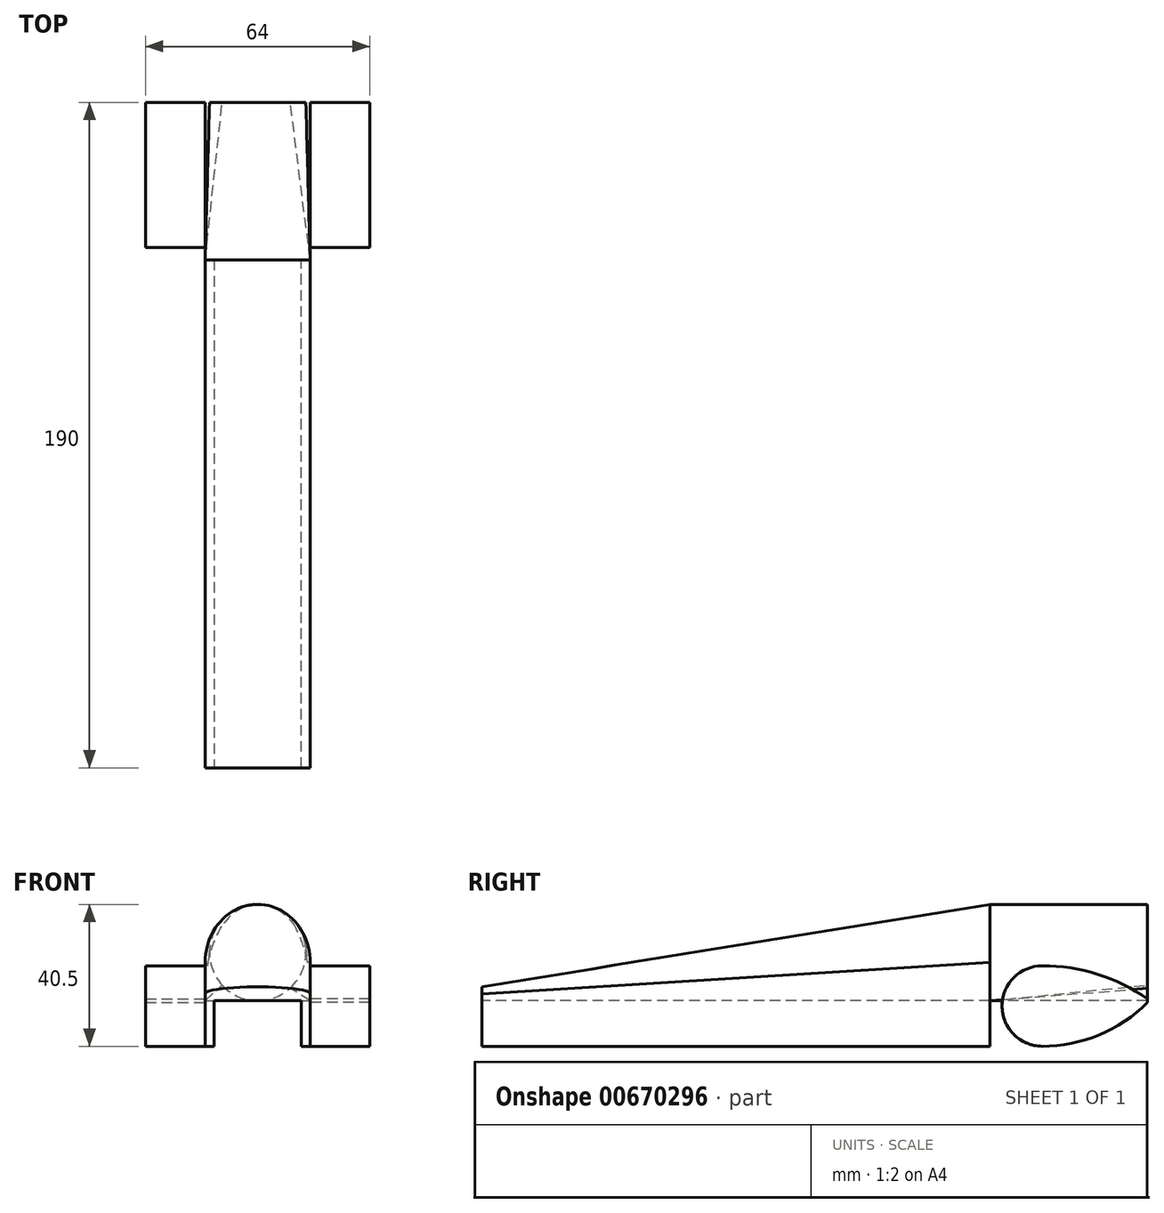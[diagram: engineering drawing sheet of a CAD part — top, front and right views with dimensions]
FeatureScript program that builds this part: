
annotation { "Feature Type Name" : "Feature", "Feature Type Description" : "" }
export const myFeature = defineFeature(function(context is Context, id is Id, definition is map)
    precondition{}
    {
        {
            var Q0;
            Q0=qCreatedBy(makeId("Front.planeOp"),FACE);
            cPlane(context, id + "F0", {"entities" : qUnion([Q0]), "cplaneType" : CPlaneType.OFFSET, "offset" : 190 * mm, "oppositeDirection" : true, "width" : 150 * mm, "height" : 150 * mm});
        }
        {
            var Q0;
            Q0=qCreatedBy(makeId("Front.planeOp"),FACE);
            cPlane(context, id + "F1", {"entities" : qUnion([Q0]), "cplaneType" : CPlaneType.OFFSET, "offset" : 145 * mm, "oppositeDirection" : true, "width" : 150 * mm, "height" : 150 * mm});
        }
        {
            var Q0;
            Q0=qCreatedBy(id+"F0.planeOp",FACE);
            var sketch = newSketch(context, id + "F2", { "sketchPlane" : qUnion([Q0])});
            skCircle(sketch, "E0", {"center": v(0, 29.75) * mm, "radius": 13.75 * mm});
            skSolve(sketch);
        }
        {
            var Q0;
            Q0=qCreatedBy(id+"F1.planeOp",FACE);
            var sketch = newSketch(context, id + "F3", { "sketchPlane" : qUnion([Q0])});
            skLineSegment(sketch, "E1", {"start": v(-15, 16) * mm, "end": v(15, 16) * mm});
            skLineSegment(sketch, "E2", {"start": v(-15, 16) * mm, "end": v(-15, 27) * mm});
            skLineSegment(sketch, "E3", {"start": v(15, 16) * mm, "end": v(15, 27) * mm});
            skEllipticalArc(sketch, "E4", {});
            skPoint(sketch, "E5.start.orphan", {"position": v(0, 16) * mm});
            const initialGuessF3  = {"E4": [0, 0.027, -1, 0, 0.015, 0.0165, 3.141592653589793, 6.283185307179586]};
            skSetInitialGuess(sketch, initialGuessF3);
            skSolve(sketch);
        }
        {
            var Q0;
            Q0=qCreatedBy(makeId("Front.planeOp"),FACE);
            var sketch = newSketch(context, id + "F4", { "sketchPlane" : qUnion([Q0])});
            skLineSegment(sketch, "E6.bottom", {"start": v(-15, 16) * mm, "end": v(15, 16) * mm});
            skLineSegment(sketch, "E6.left", {"start": v(-15, 16) * mm, "end": v(-15, 18) * mm});
            skLineSegment(sketch, "E6.right", {"start": v(15, 16) * mm, "end": v(15, 18) * mm});
            skEllipticalArc(sketch, "E7", {});
            const initialGuessF4  = {"E7": [0, 0.018, -1, 0, 0.015, 0.002, 3.141592653589793, 0]};
            skSetInitialGuess(sketch, initialGuessF4);
            skSolve(sketch);
        }
        {
            var Q0;
            Q0=makeQuery(id+"F4.imprint","IMPRINT",FACE,{"disambiguationData":[TD([[makeQuery(id+"F4.imprint","IMPRINT",EDGE,{"derivedFrom":sQuery(id+"F4.wireOp",EDGE,"E6.bottom")}),1.0]])]});
            var Q1;
            Q1=makeQuery(id+"F3.imprint","IMPRINT",FACE,{"disambiguationData":[TD([[makeQuery(id+"F3.imprint","IMPRINT",EDGE,{"derivedFrom":sQuery(id+"F3.wireOp",EDGE,"E1")}),1.0]])]});
            loft(context, id + "F5", {"sheetProfilesArray" : [{ "sheetProfileEntities" : qUnion([Q0]) }, { "sheetProfileEntities" : qUnion([Q1]) }]});
        }
        {
            var Q1;
            Q1=makeQuery(id+"F5.opLoft","CAP_FACE",FACE,{"disambiguationData":[OSD([makeQuery(id+"F3.imprint","IMPRINT",FACE,{"disambiguationData":[TD([[makeQuery(id+"F3.imprint","IMPRINT",EDGE,{"derivedFrom":sQuery(id+"F3.wireOp",EDGE,"E1")}),1.0]])]})])],"isStart":true});
            var Q2;
            Q2=makeQuery(id+"F2.imprint","IMPRINT",FACE,{"disambiguationData":[TD([[makeQuery(id+"F2.imprint","IMPRINT",EDGE,{"derivedFrom":sQuery(id+"F2.wireOp",EDGE,"E0")}),1.0]])]});
            loft(context, id + "F6", {"operationType" : NewBodyOperationType.ADD, "sheetProfilesArray" : [{ "sheetProfileEntities" : qUnion([Q1]) }, { "sheetProfileEntities" : qUnion([Q2]) }]});
        }
        {
            var Q0;
            Q0=makeQuery(id+"F5.opLoft","SWEPT_FACE",FACE,{"disambiguationData":[OSD([sQuery(id+"F3.wireOp",EDGE,"E1"),sQuery(id+"F3.wireOp",EDGE,"E2"),sQuery(id+"F3.wireOp",EDGE,"E3"),sQuery(id+"F4.wireOp",EDGE,"E6.bottom"),sQuery(id+"F4.wireOp",EDGE,"E6.left"),sQuery(id+"F4.wireOp",EDGE,"E6.right")])]});
            var sketch = newSketch(context, id + "F7", { "sketchPlane" : qUnion([Q0])});
            skLineSegment(sketch, "E8.bottom", {"start": v(15, 0) * mm, "end": v(12.5, 0) * mm});
            skLineSegment(sketch, "E8.top", {"start": v(15, -145) * mm, "end": v(12.5, -145) * mm});
            skLineSegment(sketch, "E8.left", {"start": v(15, 0) * mm, "end": v(15, -145) * mm});
            skLineSegment(sketch, "E8.right", {"start": v(12.5, 0) * mm, "end": v(12.5, -145) * mm});
            skLineSegment(sketch, "E9.bottom", {"start": v(-15, -145) * mm, "end": v(-12.5, -145) * mm});
            skLineSegment(sketch, "E9.top", {"start": v(-15, 0) * mm, "end": v(-12.5, 0) * mm});
            skLineSegment(sketch, "E9.left", {"start": v(-15, -145) * mm, "end": v(-15, 0) * mm});
            skLineSegment(sketch, "E9.right", {"start": v(-12.5, -145) * mm, "end": v(-12.5, 0) * mm});
            skSolve(sketch);
        }
        {
            var Q0;
            Q0=makeQuery(id+"F7.imprint","IMPRINT",FACE,{"disambiguationData":[TD([[makeQuery(id+"F7.imprint","IMPRINT",EDGE,{"derivedFrom":sQuery(id+"F7.wireOp",EDGE,"E8.bottom")}),1.0]])]});
            var Q1;
            Q1=makeQuery(id+"F7.imprint","IMPRINT",FACE,{"disambiguationData":[TD([[makeQuery(id+"F7.imprint","IMPRINT",EDGE,{"derivedFrom":sQuery(id+"F7.wireOp",EDGE,"E9.bottom")}),-1.0]])]});
            extrude(context, id + "F8", {"entities" : qUnion([Q0, Q1]), "operationType" : NewBodyOperationType.ADD, "depth" : 13 * mm, "offsetDistance" : 25 * mm});
        }
        {
            var Q0;
            Q0=makeQuery(id+"F8.boolean.opBoolean","MERGE",FACE,{"derivedFrom":[makeQuery(id+"F5.opLoft","SWEPT_FACE",FACE,{"disambiguationData":[OSD([sQuery(id+"F3.wireOp",EDGE,"E1"),sQuery(id+"F3.wireOp",EDGE,"E3"),sQuery(id+"F3.wireOp",EDGE,"E4"),sQuery(id+"F4.wireOp",EDGE,"E6.bottom"),sQuery(id+"F4.wireOp",EDGE,"E6.right"),sQuery(id+"F4.wireOp",EDGE,"E7")])]}),makeQuery(id+"F8.opExtrude","SWEPT_FACE",FACE,{"disambiguationData":[OSD([sQuery(id+"F7.wireOp",EDGE,"E8.left")])]})]});
            var sketch = newSketch(context, id + "F9", { "sketchPlane" : qUnion([Q0])});
            skArc(sketch, "E10", {"start": v(160, 26) * mm, "mid": v(148.5, 14.5) * mm, "end": v(160, 3) * mm});
            skLineSegment(sketch, "E11", {"start": v(190, 16.5) * mm, "end": v(190, 15.5) * mm});
            skPoint(sketch, "E12", {"position": v(160, 26) * mm});
            skArc(sketch, "E13", {"start": v(190, 16.5) * mm, "mid": v(175.73, 23.57) * mm, "end": v(160, 26) * mm});
            skArc(sketch, "E14", {"start": v(160, 3) * mm, "mid": v(176.25, 6.25) * mm, "end": v(190, 15.5) * mm});
            skSolve(sketch);
        }
        {
            var Q0;
            Q0=makeQuery(id+"F9.imprint","IMPRINT",FACE,{"disambiguationData":[TD([[makeQuery(id+"F9.imprint","IMPRINT",EDGE,{"derivedFrom":sQuery(id+"F9.wireOp",EDGE,"E10")}),1.0]])]});
            extrude(context, id + "F10", {"entities" : qUnion([Q0]), "depth" : 17 * mm, "offsetDistance" : 25 * mm});
        }
        {
            var Q0;
            Q0=makeQuery(id+"F10.opExtrude","SWEPT_BODY",BODY,{"disambiguationData":[OSD([sQuery(id+"F9.wireOp",EDGE,"E10"),sQuery(id+"F9.wireOp",EDGE,"E11"),sQuery(id+"F9.wireOp",EDGE,"E13"),sQuery(id+"F9.wireOp",EDGE,"E14")])]});
            var Q1;
            Q1=qCreatedBy(makeId("Right.planeOp"),FACE);
            mirror(context, id + "F11", {"operationType" : NewBodyOperationType.ADD, "entities" : qUnion([Q0]), "mirrorPlane" : qUnion([Q1])});
        }
    });
